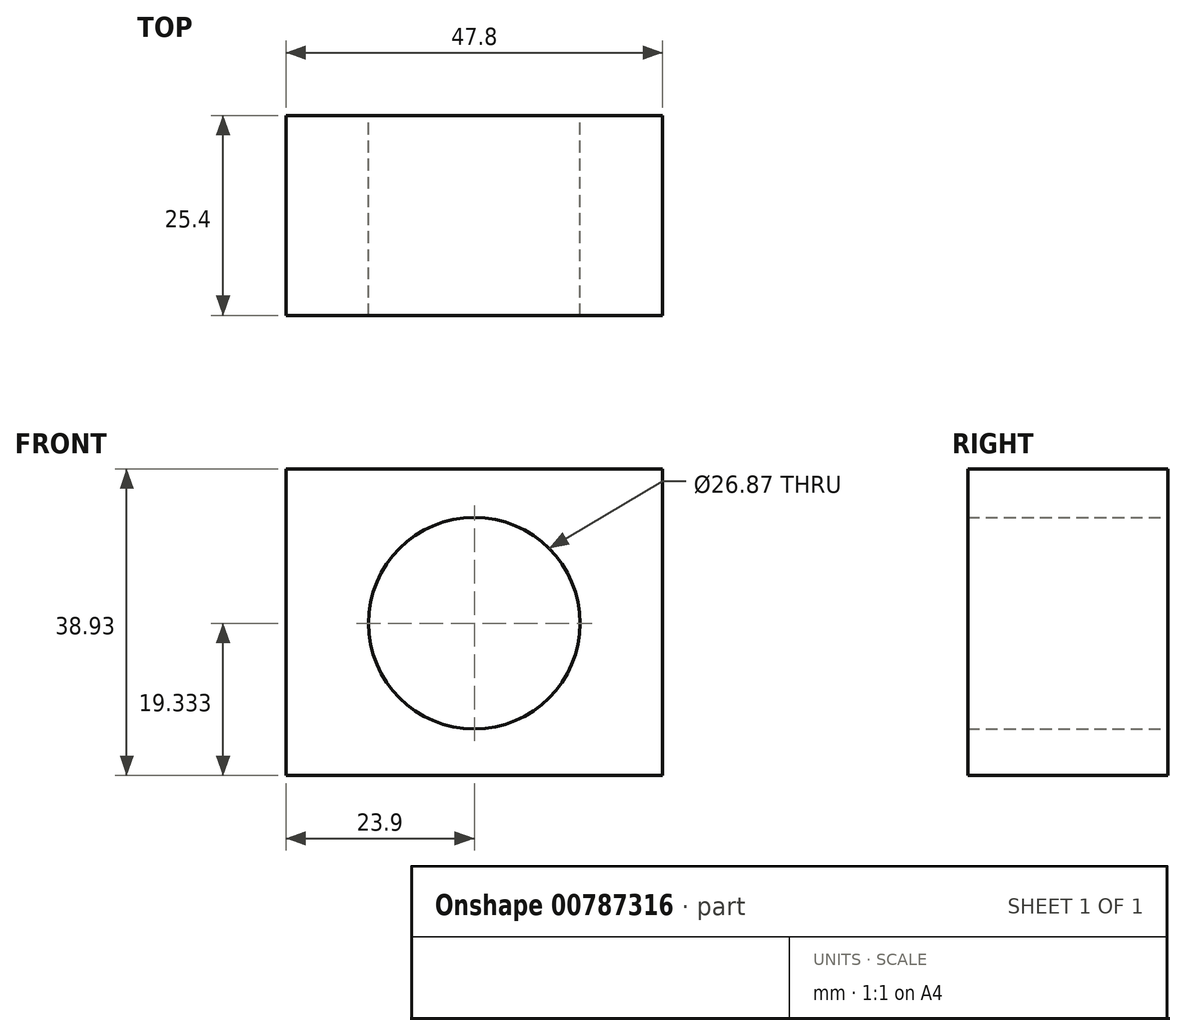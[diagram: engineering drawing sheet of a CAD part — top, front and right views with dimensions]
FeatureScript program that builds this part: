
annotation { "Feature Type Name" : "Feature", "Feature Type Description" : "" }
export const myFeature = defineFeature(function(context is Context, id is Id, definition is map)
    precondition{}
    {
        {
            var Q0;
            Q0=qCreatedBy(makeId("Front.planeOp"),FACE);
            var sketch = newSketch(context, id + "F0", { "sketchPlane" : qUnion([Q0])});
            skLineSegment(sketch, "E0.bottom", {"start": v(-65.65, 57.32) * mm, "end": v(-17.85, 57.32) * mm});
            skLineSegment(sketch, "E0.top", {"start": v(-65.65, 18.4) * mm, "end": v(-17.85, 18.4) * mm});
            skLineSegment(sketch, "E0.left", {"start": v(-65.65, 57.32) * mm, "end": v(-65.65, 18.4) * mm});
            skLineSegment(sketch, "E0.right", {"start": v(-17.85, 57.32) * mm, "end": v(-17.85, 18.4) * mm});
            skCircle(sketch, "E1", {"center": v(-41.75, 37.72) * mm, "radius": 13.44 * mm});
            skCircle(sketch, "E2", {"center": v(-41.75, 37.72) * mm, "radius": 9.76 * mm});
            skSolve(sketch);
        }
        {
            var Q0;
            Q0=makeQuery(id+"F0.imprint","IMPRINT",FACE,{"disambiguationData":[TD([[makeQuery(id+"F0.imprint","IMPRINT",EDGE,{"derivedFrom":sQuery(id+"F0.wireOp",EDGE,"E0.bottom")}),-1.0]])]});
            extrude(context, id + "F1", {"entities" : qUnion([Q0]), "depth" : 25.4 * mm, "offsetDistance" : 25.4 * mm});
        }
        {
            var Q0;
            Q0=sQuery(id+"F0.wireOp",EDGE,"E2");
            var Q1;
            Q1=sQuery(id+"F0.wireOp",EDGE,"E1");
            extrude(context, id + "F2", {"bodyType" : ToolBodyType.SURFACE, "surfaceEntities" : qUnion([Q0, Q1]), "depth" : 38.1 * mm, "offsetDistance" : 25.4 * mm});
        }
    });
